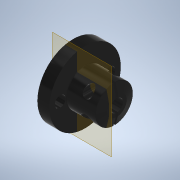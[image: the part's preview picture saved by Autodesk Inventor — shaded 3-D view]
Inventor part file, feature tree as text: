
AUTODESK INVENTOR PART (.ipt)
format: ipt  version: 2022 (Build 260153000, 153)  size: 236,032 bytes
history: native  units: in
note: dims shown in document units (in); Inventor stores cm internally (conversion verified against a paired STEP export)
features: sketch x5, extrude x4, revolve x1, fillet x1, plane x1, pattern_circular x1
ambient origin geometry x8: Origin, YZ Plane, XZ Plane, XY Plane, X Axis, Y Axis, Z Axis, Center Point
bodies: Solid1 (feature_tree)
feature tree (13):
  revolve  "Revolution1"  [1 undecoded]
  fillet  "Fillet1"  Radius=0.125in
  extrude  "Extrusion1"  Depth=0.45in
  extrude  "Extrusion2"  Depth=0.2358in
  plane  "Work Plane1"
  extrude  "Extrusion3"  Depth=0.0787in
  pattern_circular  "Circular Pattern1"  [2 undecoded]
  extrude  "Extrusion4"  Depth=0.0063in
  sketch  "Sketch1"  dims[d0=0.675in d1=0.125in d2=0.125in]
  sketch  "Sketch2"  dims[d3=0.15in d4=0.45in]
  sketch  "Sketch3"  dims[d5=0.4in d6=0.2358in]
  sketch  "Sketch4"  dims[d7=0.25in d8=0.0787in]
  sketch  "Sketch5"  dims[d9=360.0deg d10=0.125in d11=0.3685in d12=0.0063in d13=0.225in d14=0.15in d15=0.1181in d16=0.0in d17=0.0in d18=0.5in d19=0.025in d20=0.0in d21=0.1in d22=0.1575in d23=0.225in d25=0.15in d26=0.0in d27=0.0in d28=0.7874in d29=360.0deg d31=0.625in d32=0.138in d33=0.138in d34=0.0in d35=0.0in]
note: 3 required parameter values undecoded (feature->parameter linkage not recoverable at this tier; creation-order binding heuristic only, values carry confidence <= 0.55)